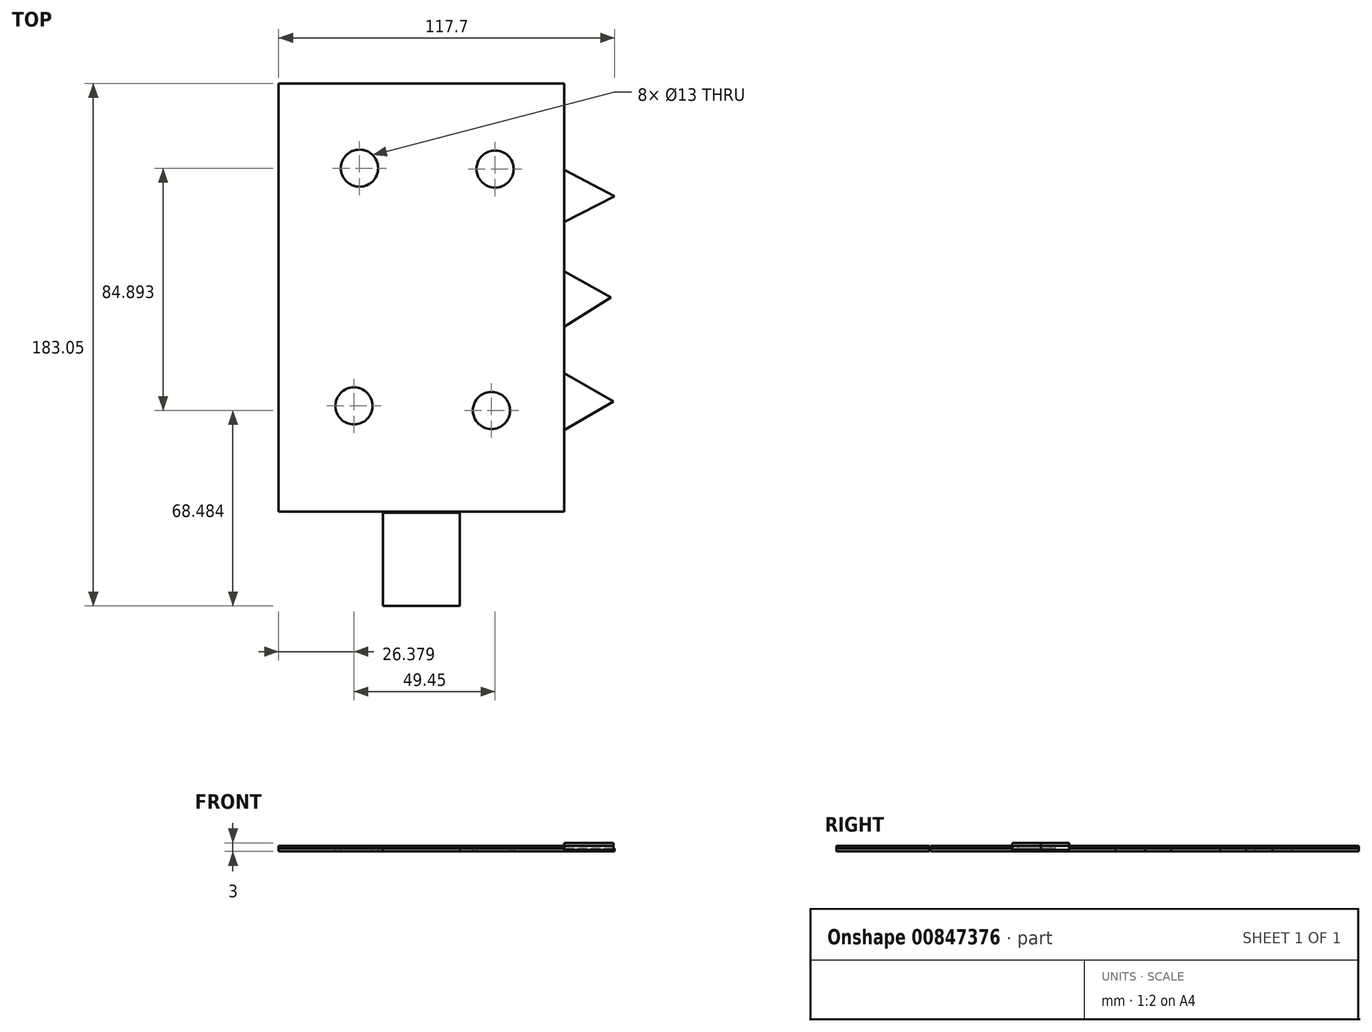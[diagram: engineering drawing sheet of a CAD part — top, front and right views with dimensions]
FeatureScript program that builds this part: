
annotation { "Feature Type Name" : "Feature", "Feature Type Description" : "" }
export const myFeature = defineFeature(function(context is Context, id is Id, definition is map)
    precondition{}
    {
        {
            var Q0;
            Q0=qCreatedBy(makeId("Top.planeOp"),FACE);
            var sketch = newSketch(context, id + "F0", { "sketchPlane" : qUnion([Q0])});
            skLineSegment(sketch, "E0.bottom", {"start": v(-50, 75) * mm, "end": v(50, 75) * mm});
            skLineSegment(sketch, "E0.top", {"start": v(-50, -75) * mm, "end": v(50, -75) * mm});
            skLineSegment(sketch, "E0.left", {"start": v(-50, 75) * mm, "end": v(-50, -75) * mm});
            skLineSegment(sketch, "E0.right", {"start": v(50, 75) * mm, "end": v(50, -75) * mm});
            skPoint(sketch, "E0.middle", {"position": v(0, 0) * mm});
            skSolve(sketch);
        }
        {
            var Q0;
            Q0=makeQuery(id+"F0.imprint","IMPRINT",FACE,{"disambiguationData":[TD([[makeQuery(id+"F0.imprint","IMPRINT",EDGE,{"derivedFrom":sQuery(id+"F0.wireOp",EDGE,"E0.bottom")}),-1.0]])]});
            var sketch = newSketch(context, id + "F1", { "sketchPlane" : qUnion([Q0])});
            skLineSegment(sketch, "E1", {"start": v(49.98, 44.73) * mm, "end": v(67.7, 35.45) * mm});
            skLineSegment(sketch, "E2", {"start": v(67.7, 35.45) * mm, "end": v(49.85, 26.42) * mm});
            skLineSegment(sketch, "E3", {"start": v(157.52, 0) * mm, "end": v(151.97, 2.9) * mm});
            skLineSegment(sketch, "E4", {"start": v(151.97, 2.9) * mm, "end": v(157.52, 0) * mm});
            skSolve(sketch);
        }
        {
            var Q0;
            Q0=makeQuery(id+"F0.imprint","IMPRINT",FACE,{"disambiguationData":[TD([[makeQuery(id+"F0.imprint","IMPRINT",EDGE,{"derivedFrom":sQuery(id+"F0.wireOp",EDGE,"E0.bottom")}),-1.0]])]});
            var sketch = newSketch(context, id + "F2", { "sketchPlane" : qUnion([Q0])});
            skLineSegment(sketch, "E5", {"start": v(49, 9.74) * mm, "end": v(66.47, 0) * mm});
            skLineSegment(sketch, "E6", {"start": v(66.47, 0) * mm, "end": v(49.48, -10.55) * mm});
            skSolve(sketch);
        }
        {
            var Q0;
            Q0=makeQuery(id+"F0.imprint","IMPRINT",FACE,{"disambiguationData":[TD([[makeQuery(id+"F0.imprint","IMPRINT",EDGE,{"derivedFrom":sQuery(id+"F0.wireOp",EDGE,"E0.bottom")}),-1.0]])]});
            var sketch = newSketch(context, id + "F3", { "sketchPlane" : qUnion([Q0])});
            skCircle(sketch, "E7", {"center": v(-21.7, 45.21) * mm, "radius": 6.5 * mm});
            skCircle(sketch, "E8", {"center": v(-21.12, -40.24) * mm, "radius": 6.5 * mm});
            skSolve(sketch);
        }
        {
            var Q0;
            {var subQ1=makeQuery(id+"F0.imprint","IMPRINT",EDGE,{"derivedFrom":sQuery(id+"F0.wireOp",EDGE,"E0.bottom")});Q0=makeQuery(id+"F2.imprint","IMPRINT",FACE,{"disambiguationData":[TD([[makeQuery(id+"F2.imprint","IMPRINT",EDGE,{"derivedFrom":subQ1}),-1.0]])]});}
            var sketch = newSketch(context, id + "F4", { "sketchPlane" : qUnion([Q0])});
            skSolve(sketch);
        }
        {
            var Q0;
            {var subQ1=makeQuery(id+"F0.imprint","IMPRINT",EDGE,{"derivedFrom":sQuery(id+"F0.wireOp",EDGE,"E0.bottom")});Q0=makeQuery(id+"F4.imprint","IMPRINT",FACE,{"disambiguationData":[TD([[makeQuery(id+"F4.imprint","IMPRINT",EDGE,{"derivedFrom":makeQuery(id+"F2.imprint","IMPRINT",EDGE,{"derivedFrom":subQ1})}),-1.0]])]});}
            var sketch = newSketch(context, id + "F5", { "sketchPlane" : qUnion([Q0])});
            skCircle(sketch, "E9", {"center": v(25.83, 45.03) * mm, "radius": 6.5 * mm});
            skCircle(sketch, "E10", {"center": v(24.56, -39.57) * mm, "radius": 6.5 * mm});
            skSolve(sketch);
        }
        {
            var Q0;
            {var subQ1=makeQuery(id+"F0.imprint","IMPRINT",EDGE,{"derivedFrom":sQuery(id+"F0.wireOp",EDGE,"E0.bottom")});Q0=makeQuery(id+"F4.imprint","IMPRINT",FACE,{"disambiguationData":[TD([[makeQuery(id+"F4.imprint","IMPRINT",EDGE,{"derivedFrom":makeQuery(id+"F2.imprint","IMPRINT",EDGE,{"derivedFrom":subQ1})}),-1.0]])]});}
            var sketch = newSketch(context, id + "F6", { "sketchPlane" : qUnion([Q0])});
            skLineSegment(sketch, "E11.bottom", {"start": v(13.5, -75.43) * mm, "end": v(-13.5, -75.43) * mm});
            skLineSegment(sketch, "E11.top", {"start": v(13.5, -108.05) * mm, "end": v(-13.5, -108.05) * mm});
            skLineSegment(sketch, "E11.left", {"start": v(13.5, -75.43) * mm, "end": v(13.5, -108.05) * mm});
            skLineSegment(sketch, "E11.right", {"start": v(-13.5, -75.43) * mm, "end": v(-13.5, -108.05) * mm});
            skPoint(sketch, "E11.middle", {"position": v(0, -91.74) * mm});
            skLineSegment(sketch, "E12.bottom", {"start": v(91.78, -121.95) * mm, "end": v(77.88, -121.95) * mm});
            skLineSegment(sketch, "E12.top", {"start": v(91.78, -116.51) * mm, "end": v(77.88, -116.51) * mm});
            skLineSegment(sketch, "E12.left", {"start": v(91.78, -121.95) * mm, "end": v(91.78, -116.51) * mm});
            skLineSegment(sketch, "E12.right", {"start": v(77.88, -121.95) * mm, "end": v(77.88, -116.51) * mm});
            skPoint(sketch, "E12.middle", {"position": v(84.83, -119.23) * mm});
            skSolve(sketch);
        }
        {
            var Q0;
            {var subQ0=sQuery(id+"F1.wireOp",EDGE,"E2");var subQ1=sQuery(id+"F1.wireOp",EDGE,"E1");var subQ2=makeQuery(id+"F1.imprint","INTERSECT",VERTEX,{"derivedFrom":[subQ1,subQ0]});Q0=makeQuery(id+"F1.imprint","IMPRINT",FACE,{"disambiguationData":[TD([[makeQuery(id+"F1.imprint","IMPRINT",EDGE,{"disambiguationData":[TD([[subQ2,1.0]])],"derivedFrom":subQ1}),-1.0]])]});}
            var Q1;
            {var subQ0=sQuery(id+"F2.wireOp",EDGE,"E6");var subQ1=sQuery(id+"F2.wireOp",EDGE,"E5");var subQ2=makeQuery(id+"F2.imprint","INTERSECT",VERTEX,{"derivedFrom":[subQ1,subQ0]});Q1=makeQuery(id+"F2.imprint","IMPRINT",FACE,{"disambiguationData":[TD([[makeQuery(id+"F2.imprint","IMPRINT",EDGE,{"disambiguationData":[TD([[subQ2,1.0]])],"derivedFrom":subQ1}),-1.0]])]});}
            extrude(context, id + "F7", {"entities" : qUnion([Q0, Q1]), "depth" : 1 * mm, "offsetDistance" : 25 * mm});
        }
        {
            var Q0;
            {var subQ1=makeQuery(id+"F0.imprint","IMPRINT",EDGE,{"derivedFrom":sQuery(id+"F0.wireOp",EDGE,"E0.bottom")});Q0=makeQuery(id+"F4.imprint","IMPRINT",FACE,{"disambiguationData":[TD([[makeQuery(id+"F4.imprint","IMPRINT",EDGE,{"derivedFrom":makeQuery(id+"F2.imprint","IMPRINT",EDGE,{"derivedFrom":subQ1})}),-1.0]])]});}
            var sketch = newSketch(context, id + "F8", { "sketchPlane" : qUnion([Q0])});
            skLineSegment(sketch, "E13", {"start": v(50.9, -30.84) * mm, "end": v(67.57, -41.88) * mm});
            skLineSegment(sketch, "E14", {"start": v(67.57, -41.88) * mm, "end": v(50.53, -52.35) * mm});
            skSolve(sketch);
        }
        {
            var Q0;
            Q0=makeQuery(id+"F5.imprint","IMPRINT",FACE,{"disambiguationData":[TD([[makeQuery(id+"F5.imprint","IMPRINT",EDGE,{"derivedFrom":sQuery(id+"F5.wireOp",EDGE,"E9")}),-1.0]])]});
            extrude(context, id + "F9", {"entities" : qUnion([Q0]), "depth" : 1 * mm, "offsetDistance" : 25 * mm});
        }
        {
            var Q0;
            {var subQ1=makeQuery(id+"F0.imprint","IMPRINT",EDGE,{"derivedFrom":sQuery(id+"F0.wireOp",EDGE,"E0.bottom")});Q0=makeQuery(id+"F8.imprint","IMPRINT",FACE,{"disambiguationData":[TD([[makeQuery(id+"F8.imprint","IMPRINT",EDGE,{"derivedFrom":makeQuery(id+"F4.imprint","IMPRINT",EDGE,{"derivedFrom":makeQuery(id+"F2.imprint","IMPRINT",EDGE,{"derivedFrom":subQ1})})}),-1.0]])]});}
            extrude(context, id + "F10", {"entities" : qUnion([Q0]), "operationType" : NewBodyOperationType.REMOVE, "oppositeDirection" : true, "depth" : 25 * mm, "offsetDistance" : 25 * mm});
        }
        {
            var Q0;
            Q0=makeQuery(id+"F9.opExtrude","CAP_FACE",FACE,{"disambiguationData":[OSD([sQuery(id+"F0.wireOp",EDGE,"E0.bottom"),sQuery(id+"F0.wireOp",EDGE,"E0.top"),sQuery(id+"F0.wireOp",EDGE,"E0.left"),sQuery(id+"F0.wireOp",EDGE,"E0.right"),sQuery(id+"F5.wireOp",EDGE,"E9"),sQuery(id+"F5.wireOp",EDGE,"E10")])],"isStart":false});
            var sketch = newSketch(context, id + "F11", { "sketchPlane" : qUnion([Q0])});
            skCircle(sketch, "E15", {"center": v(-21.67, 45.33) * mm, "radius": 6.5 * mm});
            skSolve(sketch);
        }
        {
            var Q0;
            Q0=makeQuery(id+"F11.imprint","IMPRINT",FACE,{"disambiguationData":[TD([[makeQuery(id+"F11.imprint","IMPRINT",EDGE,{"derivedFrom":sQuery(id+"F11.wireOp",EDGE,"E15")}),1.0]])]});
            extrude(context, id + "F12", {"entities" : qUnion([Q0]), "operationType" : NewBodyOperationType.REMOVE, "oppositeDirection" : true, "depth" : 25 * mm, "offsetDistance" : 25 * mm});
        }
        {
            var Q0;
            Q0=makeQuery(id+"F3.imprint","IMPRINT",FACE,{"disambiguationData":[TD([[makeQuery(id+"F3.imprint","IMPRINT",EDGE,{"derivedFrom":sQuery(id+"F3.wireOp",EDGE,"E7")}),1.0]])]});
            extrude(context, id + "F13", {"entities" : qUnion([Q0]), "operationType" : NewBodyOperationType.REMOVE, "oppositeDirection" : true, "depth" : 25 * mm, "offsetDistance" : 25 * mm});
        }
        {
            var Q0;
            Q0=makeQuery(id+"F9.opExtrude","CAP_FACE",FACE,{"disambiguationData":[OSD([sQuery(id+"F0.wireOp",EDGE,"E0.bottom"),sQuery(id+"F0.wireOp",EDGE,"E0.top"),sQuery(id+"F0.wireOp",EDGE,"E0.left"),sQuery(id+"F0.wireOp",EDGE,"E0.right"),sQuery(id+"F5.wireOp",EDGE,"E9"),sQuery(id+"F5.wireOp",EDGE,"E10")])],"isStart":false});
            var sketch = newSketch(context, id + "F14", { "sketchPlane" : qUnion([Q0])});
            skCircle(sketch, "E16", {"center": v(-23.62, -37.96) * mm, "radius": 6.5 * mm});
            skSolve(sketch);
        }
        {
            var Q0;
            Q0=makeQuery(id+"F14.imprint","IMPRINT",FACE,{"disambiguationData":[TD([[makeQuery(id+"F14.imprint","IMPRINT",EDGE,{"derivedFrom":sQuery(id+"F14.wireOp",EDGE,"E16")}),1.0]])]});
            extrude(context, id + "F15", {"entities" : qUnion([Q0]), "operationType" : NewBodyOperationType.REMOVE, "oppositeDirection" : true, "depth" : 25 * mm, "offsetDistance" : 25 * mm});
        }
        {
            var Q0;
            Q0=makeQuery(id+"F6.imprint","IMPRINT",FACE,{"disambiguationData":[TD([[makeQuery(id+"F6.imprint","IMPRINT",EDGE,{"derivedFrom":sQuery(id+"F6.wireOp",EDGE,"E11.bottom")}),1.0]])]});
            extrude(context, id + "F16", {"entities" : qUnion([Q0]), "depth" : 1 * mm, "offsetDistance" : 25 * mm});
        }
        {
            var Q0;
            Q0=makeQuery(id+"F16.opExtrude","CAP_FACE",FACE,{"disambiguationData":[OSD([sQuery(id+"F6.wireOp",EDGE,"E11.bottom"),sQuery(id+"F6.wireOp",EDGE,"E11.top"),sQuery(id+"F6.wireOp",EDGE,"E11.left"),sQuery(id+"F6.wireOp",EDGE,"E11.right")])],"isStart":false});
            var Q1;
            Q1=makeQuery(id+"F9.opExtrude","CAP_FACE",FACE,{"disambiguationData":[OSD([sQuery(id+"F0.wireOp",EDGE,"E0.bottom"),sQuery(id+"F0.wireOp",EDGE,"E0.top"),sQuery(id+"F0.wireOp",EDGE,"E0.left"),sQuery(id+"F0.wireOp",EDGE,"E0.right"),sQuery(id+"F5.wireOp",EDGE,"E9"),sQuery(id+"F5.wireOp",EDGE,"E10")])],"isStart":false});
            extrude(context, id + "F17", {"entities" : qUnion([Q0, Q1]), "depth" : 1 * mm, "offsetDistance" : 25 * mm});
        }
        {
            var Q0;
            Q0=makeQuery(id+"F17.opExtrude","CAP_FACE",FACE,{"disambiguationData":[OSD([sQuery(id+"F0.wireOp",EDGE,"E0.bottom"),sQuery(id+"F0.wireOp",EDGE,"E0.top"),sQuery(id+"F0.wireOp",EDGE,"E0.left"),sQuery(id+"F0.wireOp",EDGE,"E0.right"),sQuery(id+"F5.wireOp",EDGE,"E9"),sQuery(id+"F5.wireOp",EDGE,"E10")])],"isStart":false});
            var sketch = newSketch(context, id + "F18", { "sketchPlane" : qUnion([Q0])});
            skLineSegment(sketch, "E17", {"start": v(50, -26.5) * mm, "end": v(67.36, -36.43) * mm});
            skLineSegment(sketch, "E18", {"start": v(67.36, -36.43) * mm, "end": v(50, -46.37) * mm});
            skSolve(sketch);
        }
        {
            var Q0;
            {var subQ0=sQuery(id+"F18.wireOp",EDGE,"E17");Q0=makeQuery(id+"F18.imprint","IMPRINT",FACE,{"disambiguationData":[TD([[makeQuery(id+"F18.imprint","IMPRINT",EDGE,{"derivedFrom":subQ0}),-1.0]])]});}
            extrude(context, id + "F19", {"entities" : qUnion([Q0]), "depth" : 1 * mm, "offsetDistance" : 25 * mm});
        }
        {
            var Q0;
            Q0=makeQuery(id+"F19.opExtrude","CAP_FACE",FACE,{"disambiguationData":[OSD([sQuery(id+"F0.wireOp",EDGE,"E0.right"),sQuery(id+"F18.wireOp",EDGE,"E17"),sQuery(id+"F18.wireOp",EDGE,"E18")])],"isStart":false});
            extrude(context, id + "F20", {"entities" : qUnion([Q0]), "oppositeDirection" : true, "depth" : 2.5 * mm, "offsetDistance" : 25 * mm});
        }
    });
